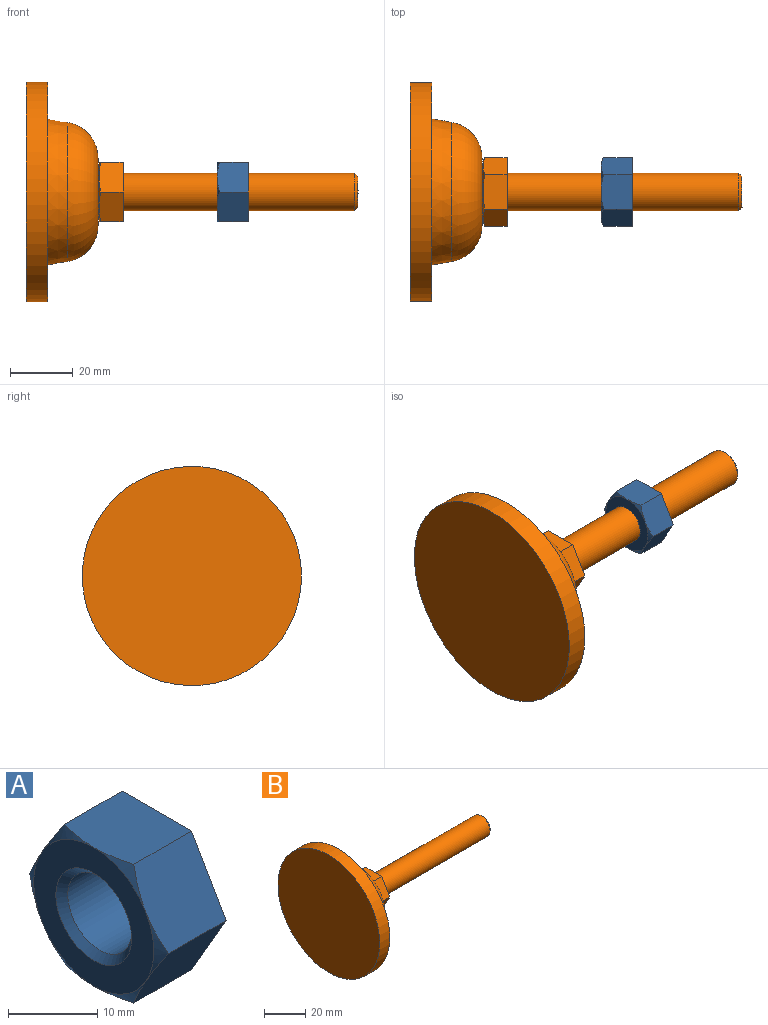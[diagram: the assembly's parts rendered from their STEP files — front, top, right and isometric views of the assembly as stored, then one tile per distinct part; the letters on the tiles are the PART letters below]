
ASSEMBLY  parts=2 mates=1
PART A: 17 faces, bbox 10x21.9x21.9 mm
  f0: plane 19x19mm, normal (-1,0,0), area 170.4mm2, adj f3,f4,f5,f7,f10,f11,f16
  f1: plane 21.94x19mm, normal (1,0,0), area 199.5mm2, adj f2,f6,f8,f9,f12,f14,f15
  f2: plane 10.97x10mm, normal (0,0,1), area 106.5mm2, adj f1,f3,f4,f8,f14
  f3: cone r=11.88mm half-angle=60deg, axis (1,0,0), area 5.6mm2, adj f0,f2,f8
  f4: cone r=11.88mm half-angle=60deg, axis (1,0,0), area 5.6mm2, adj f0,f2,f14
  f5: cone r=11.88mm half-angle=60deg, axis (1,0,0), area 5.6mm2, adj f0,f6,f8
  f6: plane 10x9.5mm, normal (0,-0.87,-0.5), area 106.5mm2, adj f1,f5,f7,f8,f9
  f7: cone r=11.88mm half-angle=60deg, axis (1,0,0), area 5.6mm2, adj f0,f6,f9
  f8: plane 10x9.5mm, normal (0,-0.87,0.5), area 106.5mm2, adj f1,f2,f3,f5,f6
  f9: plane 10.97x10mm, normal (0,0,-1), area 106.5mm2, adj f1,f6,f7,f11,f15
  f10: cone r=5.05mm half-angle=45deg, axis (-1,0,0), area 46.5mm2, adj f0,f13
  f11: cone r=11.88mm half-angle=60deg, axis (1,0,0), area 5.6mm2, adj f0,f9,f15
  f12: cone r=6mm half-angle=45deg, axis (1,0,0), area 46.5mm2, adj f1,f13
  f13: cylinder r=5.05mm len=10.11mm, axis (1,0,0), area 257.4mm2, adj f10,f12
  f14: plane 10x9.5mm, normal (0,0.87,0.5), area 106.5mm2, adj f1,f2,f4,f15,f16
  f15: plane 10x9.5mm, normal (0,0.87,-0.5), area 106.5mm2, adj f1,f9,f11,f14,f16
  f16: cone r=11.88mm half-angle=60deg, axis (1,0,0), area 5.6mm2, adj f0,f14,f15
PART B: 20 faces, bbox 106x70x70 mm
  f0: cone r=11.88mm half-angle=75.5deg, axis (1,0,0), area 115.2mm2, adj f2,f3,f7,f8,f10,f11,f12
  f1: plane 9.85x9.85mm, normal (1,0,0), area 76.2mm2, adj f6
  f2: plane 10.97x7.61mm, normal (0,0,1), area 82.1mm2, adj f0,f3,f4,f7
  f3: plane 9.5x7.61mm, normal (0,0.87,0.5), area 82.1mm2, adj f0,f2,f4,f10
  f4: plane 21.94x19mm, normal (1,0,0), area 199.5mm2, adj f2,f3,f5,f7,f10,f11,f12
  f5: cylinder r=6mm len=73.93mm, axis (1,0,0), area 2787mm2, adj f4,f6
  f6: cone r=4.93mm half-angle=45deg, axis (-1,0,0), area 52.1mm2, adj f1,f5
  f7: plane 9.5x7.61mm, normal (0,-0.87,0.5), area 82mm2, adj f0,f2,f4,f12
  f8: plane 21.45x21.45mm, normal (1,0,0), area 160.1mm2, adj f0,f9
  f9: torus R=10.72mm, axis (-1,0,0), area 1804.2mm2, adj f8,f19
  f10: plane 9.5x7.61mm, normal (0,0.87,-0.5), area 82mm2, adj f0,f3,f4,f11
  f11: plane 10.97x7.61mm, normal (0,0,-1), area 82.1mm2, adj f0,f4,f10,f12
  f12: plane 9.5x7.61mm, normal (0,-0.87,-0.5), area 82.1mm2, adj f0,f4,f7,f11
  f13: plane 70x70mm, normal (-1,0,0), area 3848.5mm2, adj f14
  f14: cylinder r=35mm len=70mm, axis (1,0,0), area 1539.4mm2, adj f13,f15
  f15: plane 70x70mm, normal (1,0,0), area 631.5mm2, adj f14,f16
  f16: cylinder r=32mm len=64mm, axis (1,0,0), area 20.1mm2, adj f15,f17
  f17: plane 64x64mm, normal (1,0,0), area 1506.6mm2, adj f16,f18
  f18: cylinder r=23.33mm len=46.67mm, axis (1,0,0), area 14.7mm2, adj f17,f19
  f19: cone r=22.21mm half-angle=10deg, axis (-1,0,0), area 923.9mm2, adj f9,f18
PLACE A t=(54.78,-2.88,1.06)mm
PLACE B t=(-6.22,-2.88,1.06)mm
MATE revolute A.f13 <-> B.f5  axis (1,0,0) through (64.78,-2.88,1.06)mm
